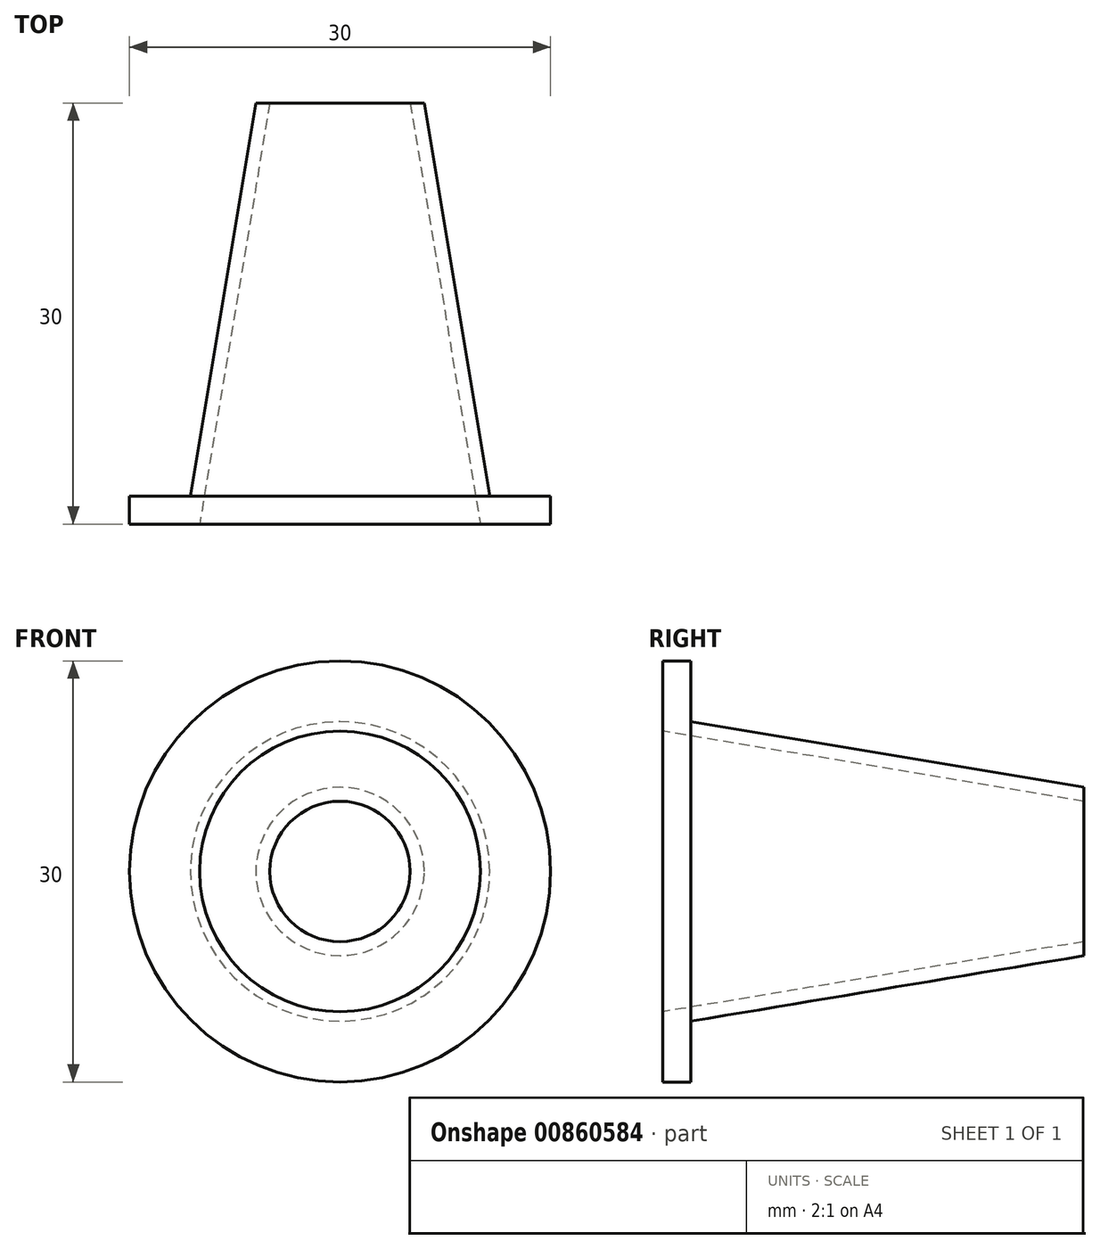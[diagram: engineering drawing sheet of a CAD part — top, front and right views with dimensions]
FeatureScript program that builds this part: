
annotation { "Feature Type Name" : "Feature", "Feature Type Description" : "" }
export const myFeature = defineFeature(function(context is Context, id is Id, definition is map)
    precondition{}
    {
        {
            var Q0;
            Q0=qCreatedBy(makeId("Front.planeOp"),FACE);
            var sketch = newSketch(context, id + "F0", { "sketchPlane" : qUnion([Q0])});
            skCircle(sketch, "E0", {"center": v(0, 0) * mm, "radius": 11 * mm});
            skSolve(sketch);
        }
        {
            var Q0;
            Q0=qCreatedBy(makeId("Front.planeOp"),FACE);
            cPlane(context, id + "F1", {"entities" : qUnion([Q0]), "cplaneType" : CPlaneType.OFFSET, "offset" : 30 * mm, "oppositeDirection" : true, "width" : 150 * mm, "height" : 150 * mm});
        }
        {
            var Q0;
            Q0=qCreatedBy(id+"F1.planeOp",FACE);
            var sketch = newSketch(context, id + "F2", { "sketchPlane" : qUnion([Q0])});
            skCircle(sketch, "E1", {"center": v(0, 0) * mm, "radius": 6 * mm});
            skSolve(sketch);
        }
        {
            var Q0;
            Q0=makeQuery(id+"F2.imprint","IMPRINT",FACE,{"disambiguationData":[TD([[makeQuery(id+"F2.imprint","IMPRINT",EDGE,{"derivedFrom":sQuery(id+"F2.wireOp",EDGE,"E1")}),1.0]])]});
            var Q1;
            Q1=makeQuery(id+"F0.imprint","IMPRINT",FACE,{"disambiguationData":[TD([[makeQuery(id+"F0.imprint","IMPRINT",EDGE,{"derivedFrom":sQuery(id+"F0.wireOp",EDGE,"E0")}),1.0]])]});
            loft(context, id + "F3", {"sheetProfilesArray" : [{ "sheetProfileEntities" : qUnion([Q0]) }, { "sheetProfileEntities" : qUnion([Q1]) }]});
        }
        {
            var Q0;
            Q0=qCreatedBy(makeId("Front.planeOp"),FACE);
            var sketch = newSketch(context, id + "F4", { "sketchPlane" : qUnion([Q0])});
            skCircle(sketch, "E2", {"center": v(0, 0) * mm, "radius": 10 * mm});
            skSolve(sketch);
        }
        {
            var Q0;
            Q0=qCreatedBy(id+"F1.planeOp",FACE);
            var sketch = newSketch(context, id + "F5", { "sketchPlane" : qUnion([Q0])});
            skCircle(sketch, "E3", {"center": v(0, 0) * mm, "radius": 5 * mm});
            skSolve(sketch);
        }
        {
            var Q0;
            Q0=qCreatedBy(makeId("Front.planeOp"),FACE);
            var sketch = newSketch(context, id + "F6", { "sketchPlane" : qUnion([Q0])});
            skCircle(sketch, "E4", {"center": v(0, 0) * mm, "radius": 15 * mm});
            skSolve(sketch);
        }
        {
            var Q0;
            Q0=makeQuery(id+"F6.imprint","IMPRINT",FACE,{"disambiguationData":[TD([[makeQuery(id+"F6.imprint","IMPRINT",EDGE,{"derivedFrom":sQuery(id+"F6.wireOp",EDGE,"E4")}),1.0]])]});
            extrude(context, id + "F7", {"entities" : qUnion([Q0]), "operationType" : NewBodyOperationType.ADD, "oppositeDirection" : true, "depth" : 2 * mm, "offsetDistance" : 25 * mm});
        }
        {
            var Q1;
            Q1=makeQuery(id+"F5.imprint","IMPRINT",FACE,{"disambiguationData":[TD([[makeQuery(id+"F5.imprint","IMPRINT",EDGE,{"derivedFrom":sQuery(id+"F5.wireOp",EDGE,"E3")}),1.0]])]});
            var Q2;
            Q2=makeQuery(id+"F4.imprint","IMPRINT",FACE,{"disambiguationData":[TD([[makeQuery(id+"F4.imprint","IMPRINT",EDGE,{"derivedFrom":sQuery(id+"F4.wireOp",EDGE,"E2")}),1.0]])]});
            loft(context, id + "F8", {"operationType" : NewBodyOperationType.REMOVE, "sheetProfilesArray" : [{ "sheetProfileEntities" : qUnion([Q1]) }, { "sheetProfileEntities" : qUnion([Q2]) }]});
        }
    });
